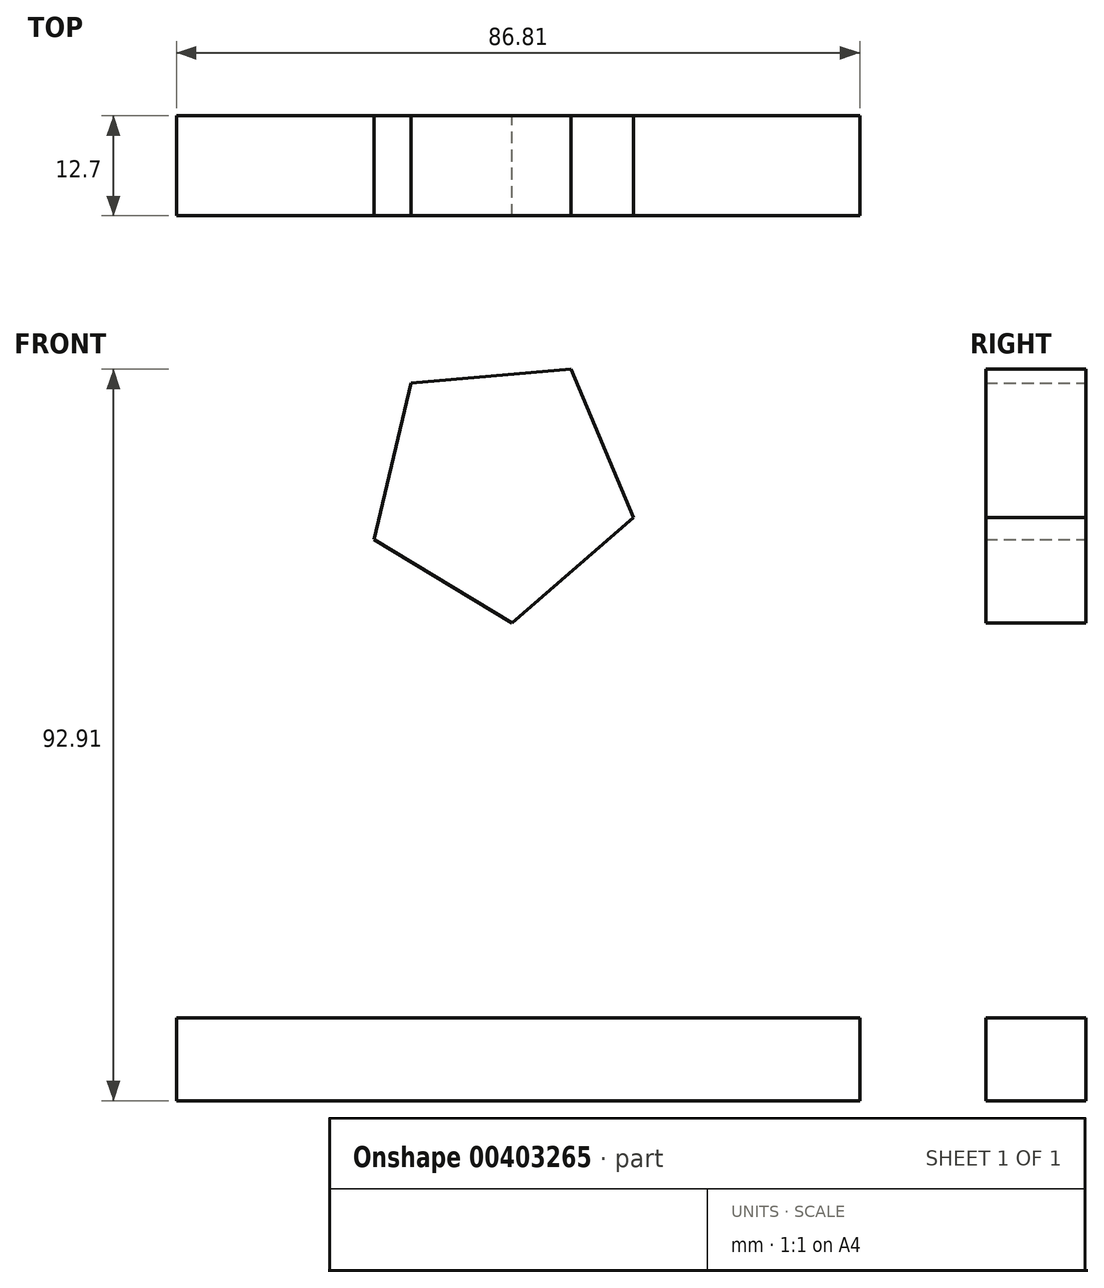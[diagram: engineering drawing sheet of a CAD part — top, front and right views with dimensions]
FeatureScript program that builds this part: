
annotation { "Feature Type Name" : "Feature", "Feature Type Description" : "" }
export const myFeature = defineFeature(function(context is Context, id is Id, definition is map)
    precondition{}
    {
        {
            var Q0;
            Q0=qCreatedBy(makeId("Front.planeOp"),FACE);
            var sketch = newSketch(context, id + "F0", { "sketchPlane" : qUnion([Q0])});
            skLineSegment(sketch, "E0.bottom", {"start": v(-41.15, -9.03) * mm, "end": v(45.66, -9.03) * mm});
            skLineSegment(sketch, "E0.top", {"start": v(-41.15, -19.57) * mm, "end": v(45.66, -19.57) * mm});
            skLineSegment(sketch, "E0.left", {"start": v(-41.15, -9.03) * mm, "end": v(-41.15, -19.57) * mm});
            skLineSegment(sketch, "E0.right", {"start": v(45.66, -9.03) * mm, "end": v(45.66, -19.57) * mm});
            skCircle(sketch, "E1.cCircle", {"center": v(0, 58.46) * mm, "radius": 14.07 * mm, "construction": true});
            skLineSegment(sketch, "E1.0", {"start": v(1.47, 41.13) * mm, "end": v(-16.03, 51.7) * mm});
            skLineSegment(sketch, "E1.1", {"start": v(-16.03, 51.7) * mm, "end": v(-11.38, 71.6) * mm});
            skLineSegment(sketch, "E1.2", {"start": v(-11.38, 71.6) * mm, "end": v(9, 73.34) * mm});
            skLineSegment(sketch, "E1.3", {"start": v(9, 73.34) * mm, "end": v(16.94, 54.5) * mm});
            skLineSegment(sketch, "E1.4", {"start": v(16.94, 54.5) * mm, "end": v(1.47, 41.13) * mm});
            skPoint(sketch, "E1.0.midPoint", {"position": v(-7.28, 46.41) * mm});
            skSolve(sketch);
        }
        {
            var Q0;
            Q0=makeQuery(id+"F0.imprint","IMPRINT",FACE,{"disambiguationData":[TD([[makeQuery(id+"F0.imprint","IMPRINT",EDGE,{"derivedFrom":sQuery(id+"F0.wireOp",EDGE,"E0.bottom")}),-1.0]])]});
            var Q1;
            Q1=makeQuery(id+"F0.imprint","IMPRINT",FACE,{"disambiguationData":[TD([[makeQuery(id+"F0.imprint","IMPRINT",EDGE,{"derivedFrom":sQuery(id+"F0.wireOp",EDGE,"E1.0")}),-1.0]])]});
            extrude(context, id + "F1", {"entities" : qUnion([Q0, Q1]), "depth" : 12.7 * mm});
        }
    });
